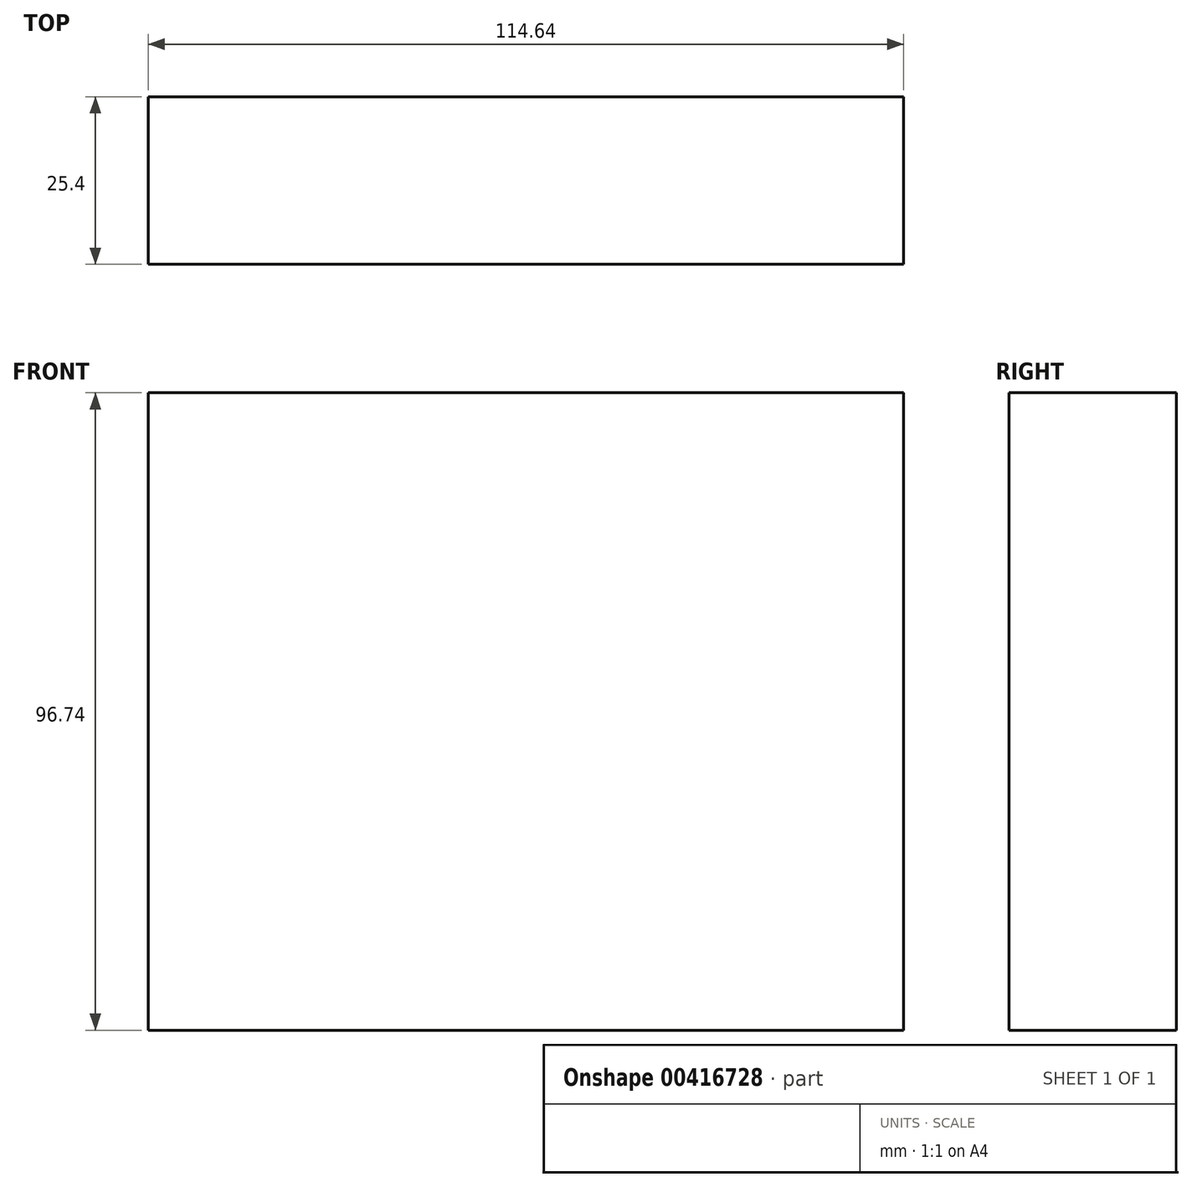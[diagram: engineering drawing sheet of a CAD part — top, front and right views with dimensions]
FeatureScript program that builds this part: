
annotation { "Feature Type Name" : "Feature", "Feature Type Description" : "" }
export const myFeature = defineFeature(function(context is Context, id is Id, definition is map)
    precondition{}
    {
        {
            var Q0;
            Q0=qCreatedBy(makeId("Front.planeOp"),FACE);
            var sketch = newSketch(context, id + "F0", { "sketchPlane" : qUnion([Q0])});
            skLineSegment(sketch, "E0.bottom", {"start": v(-39.22, 38.22) * mm, "end": v(75.42, 38.22) * mm});
            skLineSegment(sketch, "E0.top", {"start": v(-39.22, -58.52) * mm, "end": v(75.42, -58.52) * mm});
            skLineSegment(sketch, "E0.left", {"start": v(-39.22, 38.22) * mm, "end": v(-39.22, -58.52) * mm});
            skLineSegment(sketch, "E0.right", {"start": v(75.42, 38.22) * mm, "end": v(75.42, -58.52) * mm});
            skSolve(sketch);
        }
        {
            var Q0;
            Q0=makeQuery(id+"F0.imprint","IMPRINT",FACE,{"disambiguationData":[TD([[makeQuery(id+"F0.imprint","IMPRINT",EDGE,{"derivedFrom":sQuery(id+"F0.wireOp",EDGE,"E0.bottom")}),-1.0]])]});
            extrude(context, id + "F1", {"entities" : qUnion([Q0]), "depth" : 25.4 * mm, "offsetDistance" : 25.4 * mm});
        }
    });
